# Revit family: UniLED kombi ST LED 230V 1t (takmontasje)
name_source: partatom
category: Lighting Fixtures
revit_build: Autodesk Revit 2013 (Build: 20130531_2115(x64)
units: mm (PartAtom-declared; Revit-internal decimal feet)

## types (9) — shared parameters
Apparent Load = 17 VA
Body Material and Colour = Default
Color Filter = 16777215
Dimming Lamp Color Temperature Shift = <None>
Emit Shape Visible in Rendering = No
Emit from Rectangle Length = 363 mm  [stored 1.19094 ft]
Emit from Rectangle Width = 149 mm  [stored 0.488845 ft]
Height = 149 mm  [stored 0.488845 ft]
Lamp = 1
Length = 363 mm  [stored 1.19094 ft]
Length 1 = 333 mm  [stored 1.09252 ft]
Number of Poles = 1
Photometric Web File = 20x42A12.ies
Tilt Angle = 90.00°
Voltage = 230 V
Wattage Comments = 17 W
Width = 83 mm  [stored 0.27231 ft]

## per-type parameters (varying)
| type | Ledelys | ML | MarkeringsLys 45 Ned mot høyre | MarkeringsLys 45 Ned mot venstre | MarkeringsLys 45 Opp mot høyre | MarkeringsLys 45 Opp mot venstre | MarkeringsLys Høyre | MarkeringsLys Ned | MarkeringsLys Opp | MarkeringsLys Venstre |
| LedeLys | Yes | No | No | No | No | No | No | No | No | No |
| MarkeringsLys (Opp) | No | Yes | No | No | No | No | No | No | Yes | No |
| MarkeringsLys (45 Ned mot høyre) | No | Yes | Yes | No | No | No | No | No | No | No |
| MarkeringsLys (45 Ned mot venstre) | No | Yes | No | Yes | No | No | No | No | No | No |
| MarkeringsLys (45 Opp mot høyre) | No | Yes | No | No | Yes | No | No | No | No | No |
| MarkeringsLys (45 Opp mot venstre) | No | Yes | No | No | No | Yes | No | No | No | No |
| MarkeringsLys (Høyre) | No | Yes | No | No | No | No | Yes | No | No | No |
| MarkeringsLys (Venstre) | No | Yes | No | No | No | No | No | No | No | Yes |
| MarkeringsLys (Ned) | No | Yes | No | No | No | No | No | Yes | No | No |

note: [stored X ft] marks values corroborated as IEEE doubles in the binary element streams (Revit-internal decimal feet)

## geometry (parser evidence)
native form markers: Sweep x26
no freeform markers — native parametric forms only
